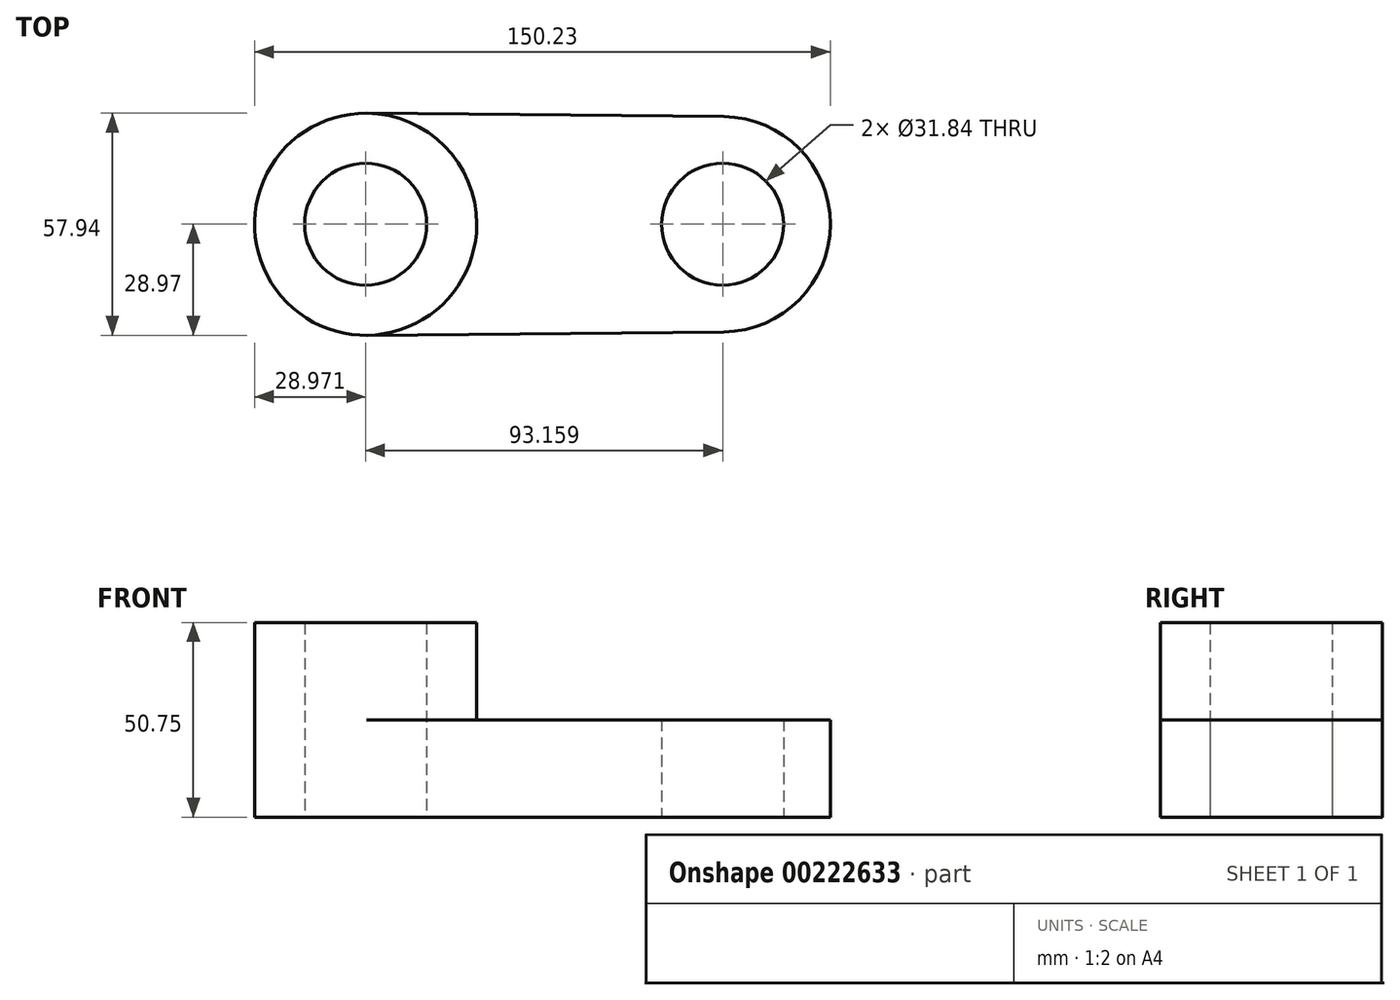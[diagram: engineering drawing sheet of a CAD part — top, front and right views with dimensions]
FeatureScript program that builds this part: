
annotation { "Feature Type Name" : "Feature", "Feature Type Description" : "" }
export const myFeature = defineFeature(function(context is Context, id is Id, definition is map)
    precondition{}
    {
        {
            var Q0;
            Q0=qCreatedBy(makeId("Top.planeOp"),FACE);
            var sketch = newSketch(context, id + "F0", { "sketchPlane" : qUnion([Q0])});
            skCircle(sketch, "E0", {"center": v(-46.58, 0) * mm, "radius": 15.92 * mm});
            skCircle(sketch, "E1", {"center": v(46.58, 0) * mm, "radius": 15.92 * mm});
            skArc(sketch, "E2", {"start": v(-46.3, 28.97) * mm, "mid": v(-75.55, 0) * mm, "end": v(-46.3, -28.97) * mm});
            skArc(sketch, "E3", {"start": v(46.84, -28.1) * mm, "mid": v(74.68, 0) * mm, "end": v(46.84, 28.1) * mm});
            skLineSegment(sketch, "E4", {"start": v(-46.3, 28.97) * mm, "end": v(46.84, 28.1) * mm});
            skLineSegment(sketch, "E5", {"start": v(46.84, -28.1) * mm, "end": v(-46.3, -28.97) * mm});
            skArc(sketch, "E6", {"start": v(-46.3, -28.97) * mm, "mid": v(-17.6, 0) * mm, "end": v(-46.3, 28.97) * mm});
            skSolve(sketch);
        }
        {
            var Q0;
            Q0=makeQuery(id+"F0.imprint","IMPRINT",FACE,{"disambiguationData":[TD([[makeQuery(id+"F0.imprint","IMPRINT",EDGE,{"derivedFrom":sQuery(id+"F0.wireOp",EDGE,"E0")}),-1.0]])]});
            var sketch = newSketch(context, id + "F1", { "sketchPlane" : qUnion([Q0])});
            skSolve(sketch);
        }
        {
            var Q0;
            Q0=makeQuery(id+"F0.imprint","IMPRINT",FACE,{"disambiguationData":[TD([[makeQuery(id+"F0.imprint","IMPRINT",EDGE,{"derivedFrom":sQuery(id+"F0.wireOp",EDGE,"E1")}),-1.0]])]});
            extrude(context, id + "F2", {"entities" : qUnion([Q0]), "depth" : 25.4 * mm});
        }
        {
            var Q0;
            Q0=makeQuery(id+"F1.imprint","IMPRINT",FACE,{"disambiguationData":[TD([[makeQuery(id+"F1.imprint","IMPRINT",EDGE,{"derivedFrom":makeQuery(id+"F0.imprint","IMPRINT",EDGE,{"derivedFrom":sQuery(id+"F0.wireOp",EDGE,"E0")})}),-1.0]])]});
            extrude(context, id + "F3", {"entities" : qUnion([Q0]), "operationType" : NewBodyOperationType.ADD, "depth" : 50.75 * mm});
        }
    });
